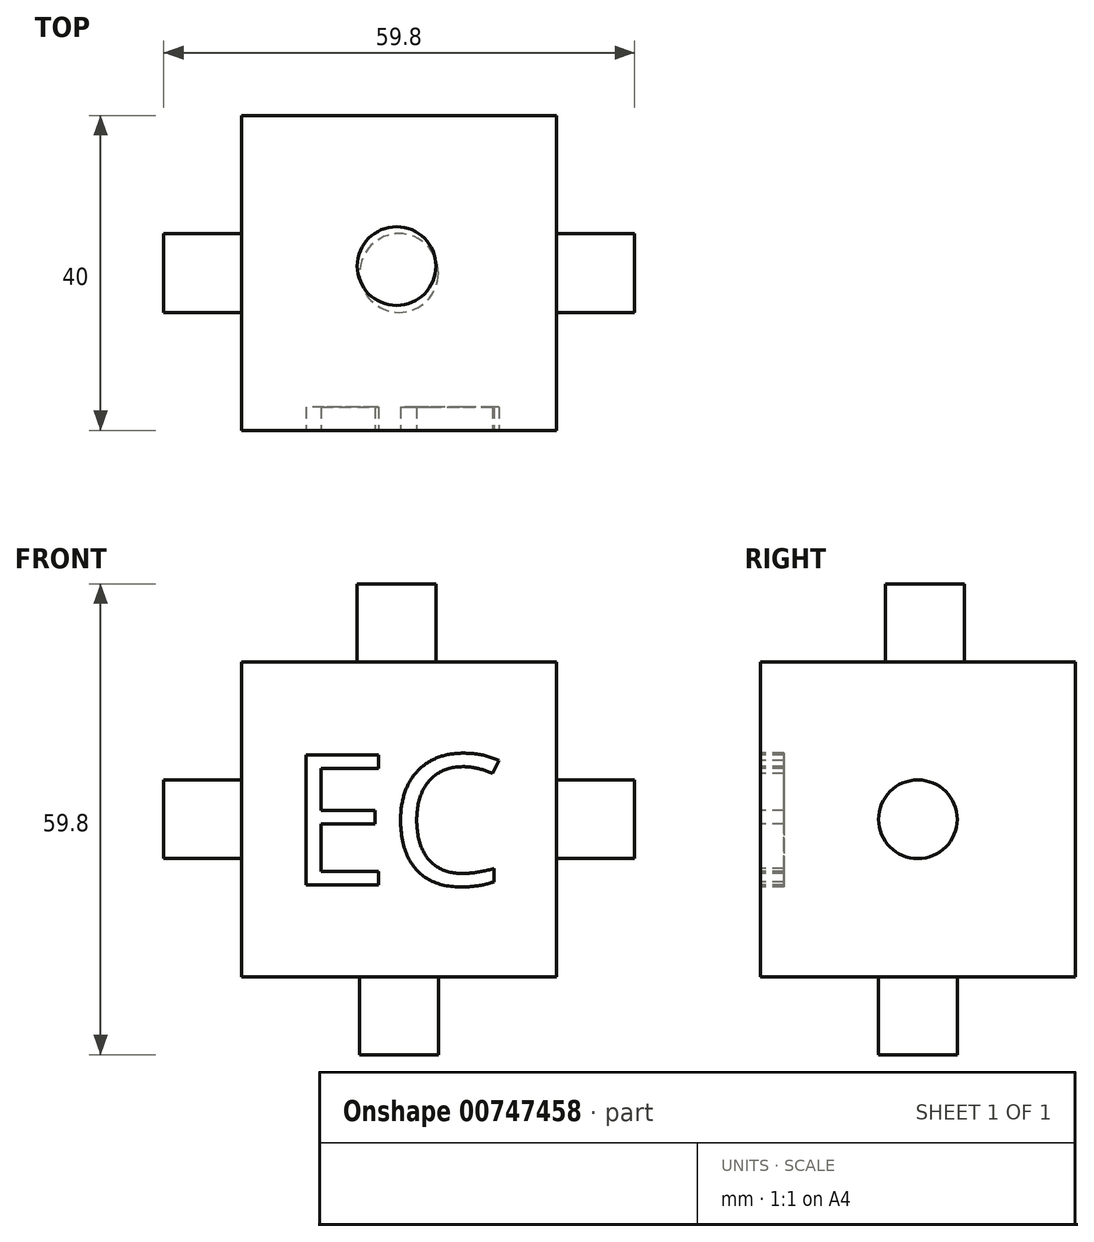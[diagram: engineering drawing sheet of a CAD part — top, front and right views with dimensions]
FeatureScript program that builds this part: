
annotation { "Feature Type Name" : "Feature", "Feature Type Description" : "" }
export const myFeature = defineFeature(function(context is Context, id is Id, definition is map)
    precondition{}
    {
        {
            var Q0;
            Q0=qCreatedBy(makeId("Front.planeOp"),FACE);
            var sketch = newSketch(context, id + "F0", { "sketchPlane" : qUnion([Q0])});
            skLineSegment(sketch, "E0", {"start": v(0, 0) * mm, "end": v(0, 40) * mm});
            skLineSegment(sketch, "E1", {"start": v(0, 40) * mm, "end": v(40, 40) * mm});
            skLineSegment(sketch, "E2", {"start": v(40, 40) * mm, "end": v(40, 0) * mm});
            skLineSegment(sketch, "E3", {"start": v(40, 0) * mm, "end": v(0, 0) * mm});
            skSolve(sketch);
        }
        {
            var Q0;
            Q0=makeQuery(id+"F0.imprint","IMPRINT",FACE,{"disambiguationData":[TD([[makeQuery(id+"F0.imprint","IMPRINT",EDGE,{"derivedFrom":sQuery(id+"F0.wireOp",EDGE,"E0")}),-1.0]])]});
            extrude(context, id + "F1", {"entities" : qUnion([Q0]), "depth" : 40 * mm, "offsetDistance" : 25 * mm});
        }
        {
            var Q0;
            Q0=makeQuery(id+"F1.opExtrude","CAP_FACE",FACE,{"disambiguationData":[OSD([sQuery(id+"F0.wireOp",EDGE,"E0"),sQuery(id+"F0.wireOp",EDGE,"E1"),sQuery(id+"F0.wireOp",EDGE,"E2"),sQuery(id+"F0.wireOp",EDGE,"E3")])],"isStart":false});
            var sketch = newSketch(context, id + "F2", { "sketchPlane" : qUnion([Q0])});
            skText(sketch, "E4", { "text": "EC", "fontName": "OpenSans-Regular.ttf"});
            const initialGuessF2  = {"E4": [0.0059, 0.01164, 1, 0, 0.01667]};
            skSetInitialGuess(sketch, initialGuessF2);
            skSolve(sketch);
        }
        {
            var Q0;
            Q0 = qSketchRegion(id + "F2", true);
            extrude(context, id + "F3", {"entities" : qUnion([Q0]), "operationType" : NewBodyOperationType.REMOVE, "oppositeDirection" : true, "depth" : 3 * mm, "offsetDistance" : 25 * mm});
        }
        {
            var Q0;
            Q0=makeQuery(id+"F1.opExtrude","SWEPT_FACE",FACE,{"disambiguationData":[OSD([sQuery(id+"F0.wireOp",EDGE,"E0")])]});
            var sketch = newSketch(context, id + "F4", { "sketchPlane" : qUnion([Q0])});
            skCircle(sketch, "E5", {"center": v(20, 20) * mm, "radius": 5 * mm});
            skPoint(sketch, "E5.centerSnap0", {"position": v(20, 40) * mm});
            skPoint(sketch, "E5.centerSnap1", {"position": v(0, 20) * mm});
            skSolve(sketch);
        }
        {
            var Q0;
            Q0 = qSketchRegion(id + "F4", true);
            extrude(context, id + "F5", {"entities" : qUnion([Q0]), "operationType" : NewBodyOperationType.ADD, "depth" : 9.9 * mm, "offsetDistance" : 25 * mm});
        }
        {
            var Q0;
            Q0=makeQuery(id+"F1.opExtrude","SWEPT_FACE",FACE,{"disambiguationData":[OSD([sQuery(id+"F0.wireOp",EDGE,"E2")])]});
            var sketch = newSketch(context, id + "F6", { "sketchPlane" : qUnion([Q0])});
            skCircle(sketch, "E6", {"center": v(-20, 20) * mm, "radius": 5 * mm});
            skPoint(sketch, "E6.centerSnap0", {"position": v(-20, 0) * mm});
            skPoint(sketch, "E6.centerSnap1", {"position": v(-40, 20) * mm});
            skSolve(sketch);
        }
        {
            var Q0;
            Q0 = qSketchRegion(id + "F6", true);
            extrude(context, id + "F7", {"entities" : qUnion([Q0]), "operationType" : NewBodyOperationType.ADD, "depth" : 9.9 * mm, "offsetDistance" : 25 * mm});
        }
        {
            var Q0;
            Q0=makeQuery(id+"F1.opExtrude","SWEPT_FACE",FACE,{"disambiguationData":[OSD([sQuery(id+"F0.wireOp",EDGE,"E1")])]});
            var sketch = newSketch(context, id + "F8", { "sketchPlane" : qUnion([Q0])});
            skCircle(sketch, "E7", {"center": v(19.69, -19.11) * mm, "radius": 5 * mm});
            skSolve(sketch);
        }
        {
            var Q0;
            Q0=makeQuery(id+"F8.imprint","IMPRINT",FACE,{"disambiguationData":[TD([[makeQuery(id+"F8.imprint","IMPRINT",EDGE,{"derivedFrom":sQuery(id+"F8.wireOp",EDGE,"E7")}),1.0]])]});
            extrude(context, id + "F9", {"entities" : qUnion([Q0]), "operationType" : NewBodyOperationType.ADD, "depth" : 9.9 * mm, "offsetDistance" : 25 * mm});
        }
        {
            var Q0;
            Q0=makeQuery(id+"F1.opExtrude","SWEPT_FACE",FACE,{"disambiguationData":[OSD([sQuery(id+"F0.wireOp",EDGE,"E3")])]});
            var sketch = newSketch(context, id + "F10", { "sketchPlane" : qUnion([Q0])});
            skCircle(sketch, "E8", {"center": v(20, 20) * mm, "radius": 5 * mm});
            skPoint(sketch, "E8.centerSnap0", {"position": v(0, 20) * mm});
            skPoint(sketch, "E8.centerSnap1", {"position": v(20, 0) * mm});
            skSolve(sketch);
        }
        {
            var Q0;
            Q0 = qSketchRegion(id + "F10", true);
            extrude(context, id + "F11", {"entities" : qUnion([Q0]), "operationType" : NewBodyOperationType.ADD, "depth" : 9.9 * mm, "offsetDistance" : 25 * mm});
        }
    });
